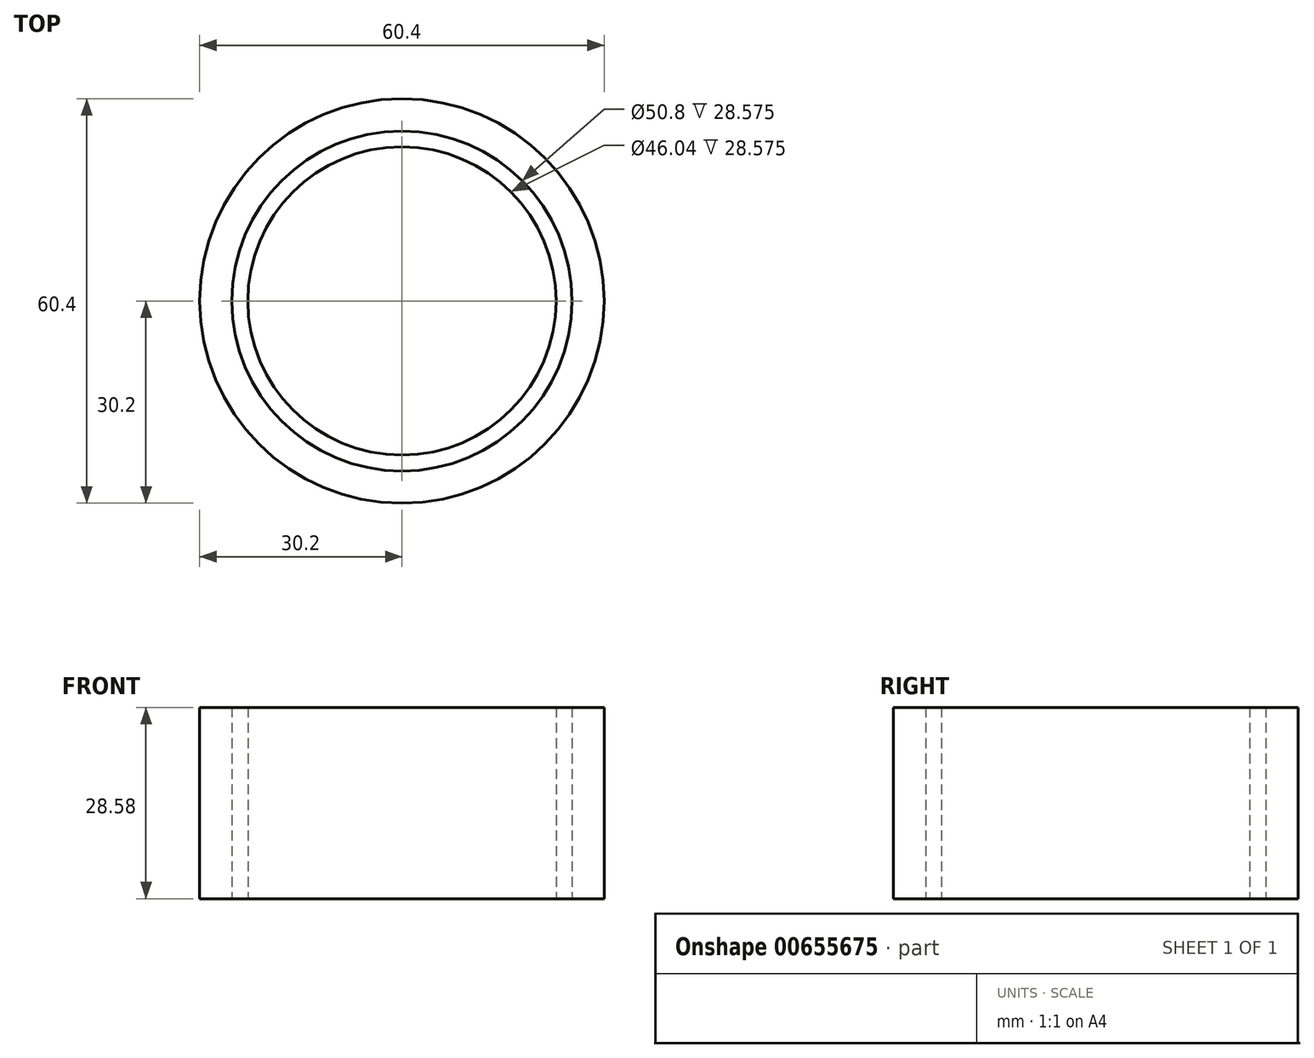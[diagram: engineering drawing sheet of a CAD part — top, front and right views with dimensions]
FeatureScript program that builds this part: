
annotation { "Feature Type Name" : "Feature", "Feature Type Description" : "" }
export const myFeature = defineFeature(function(context is Context, id is Id, definition is map)
    precondition{}
    {
        {
            var Q0;
            Q0=qCreatedBy(makeId("Top.planeOp"),FACE);
            var sketch = newSketch(context, id + "F0", { "sketchPlane" : qUnion([Q0])});
            skCircle(sketch, "E0", {"center": v(0, 0) * mm, "radius": 23.02 * mm});
            skCircle(sketch, "E1", {"center": v(0, 0) * mm, "radius": 25.4 * mm});
            skCircle(sketch, "E2", {"center": v(0, 0) * mm, "radius": 30.2 * mm});
            skSolve(sketch);
        }
        {
            var Q0;
            Q0=makeQuery(id+"F0.imprint","IMPRINT",FACE,{"disambiguationData":[TD([[makeQuery(id+"F0.imprint","IMPRINT",EDGE,{"derivedFrom":sQuery(id+"F0.wireOp",EDGE,"E0")}),1.0]])]});
            extrude(context, id + "F1", {"entities" : qUnion([Q0]), "depth" : 28.57 * mm, "offsetDistance" : 25.4 * mm});
        }
        {
            var Q0;
            Q0 = qSketchRegion(id + "F0", true);
            extrude(context, id + "F2", {"entities" : qUnion([Q0]), "depth" : 28.57 * mm, "offsetDistance" : 25.4 * mm});
        }
        {
            var Q0;
            Q0=makeQuery(id+"F0.imprint","IMPRINT",FACE,{"disambiguationData":[TD([[makeQuery(id+"F0.imprint","IMPRINT",EDGE,{"derivedFrom":sQuery(id+"F0.wireOp",EDGE,"E0")}),-1.0]])]});
            extrude(context, id + "F3", {"entities" : qUnion([Q0]), "depth" : 28.57 * mm, "offsetDistance" : 25.4 * mm});
        }
        {
            var Q0;
            Q0=makeQuery(id+"F1.opExtrude","CAP_FACE",FACE,{"disambiguationData":[OSD([sQuery(id+"F0.wireOp",EDGE,"E0")])],"isStart":false});
            extrude(context, id + "F4", {"entities" : qUnion([Q0]), "operationType" : NewBodyOperationType.REMOVE, "oppositeDirection" : true, "depth" : 76.2 * mm, "offsetDistance" : 25.4 * mm});
        }
    });
